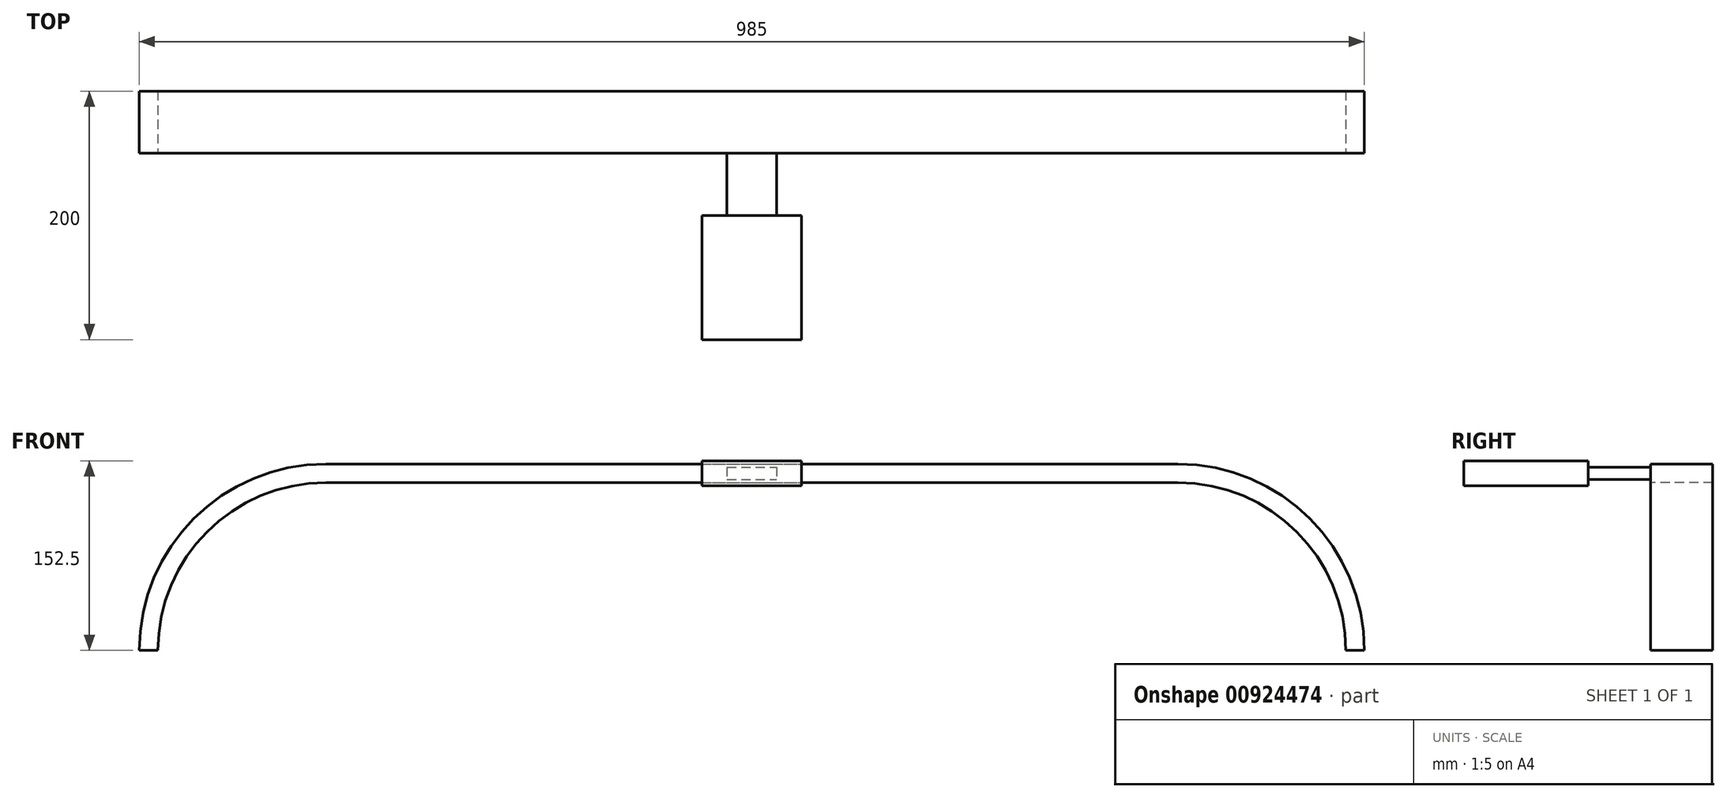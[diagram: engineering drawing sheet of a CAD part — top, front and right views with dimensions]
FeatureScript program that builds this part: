
annotation { "Feature Type Name" : "Feature", "Feature Type Description" : "" }
export const myFeature = defineFeature(function(context is Context, id is Id, definition is map)
    precondition{}
    {
        {
            var Q0;
            Q0=qCreatedBy(makeId("Top.planeOp"),FACE);
            var sketch = newSketch(context, id + "F0", { "sketchPlane" : qUnion([Q0])});
            skLineSegment(sketch, "E0.bottom", {"start": v(-7.5, 25) * mm, "end": v(7.5, 25) * mm});
            skLineSegment(sketch, "E0.top", {"start": v(-7.5, -25) * mm, "end": v(7.5, -25) * mm});
            skLineSegment(sketch, "E0.left", {"start": v(-7.5, 25) * mm, "end": v(-7.5, -25) * mm});
            skLineSegment(sketch, "E0.right", {"start": v(7.5, 25) * mm, "end": v(7.5, -25) * mm});
            skLineSegment(sketch, "E1", {"start": v(-142.5, 39) * mm, "end": v(-142.5, -46.74) * mm});
            skSolve(sketch);
        }
        {
            var Q0;
            Q0=makeQuery(id+"F0.imprint","IMPRINT",FACE,{"disambiguationData":[TD([[makeQuery(id+"F0.imprint","IMPRINT",EDGE,{"derivedFrom":sQuery(id+"F0.wireOp",EDGE,"E0.bottom")}),-1.0]])]});
            var Q1;
            Q1=sQuery(id+"F0.wireOp",EDGE,"E1");
            revolve(context, id + "F1", {"surfaceOperationType" : NewSurfaceOperationType.NEW, "entities" : qUnion([Q0]), "axis" : qUnion([Q1]), "revolveType" : RevolveType.ONE_DIRECTION, "angle" : 90 * degree});
        }
        {
            var Q0;
            Q0=makeQuery(id+"F1.opRevolve","CAP_FACE",FACE,{"disambiguationData":[OSD([sQuery(id+"F0.wireOp",EDGE,"E0.bottom"),sQuery(id+"F0.wireOp",EDGE,"E0.top"),sQuery(id+"F0.wireOp",EDGE,"E0.left"),sQuery(id+"F0.wireOp",EDGE,"E0.right")])],"isStart":false});
            extrude(context, id + "F2", {"entities" : qUnion([Q0]), "operationType" : NewBodyOperationType.ADD, "depth" : 685 * mm, "offsetDistance" : 25 * mm});
        }
        {
            var Q0;
            Q0=makeQuery(id+"F2.opExtrude","CAP_FACE",FACE,{"disambiguationData":[OSD([sQuery(id+"F0.wireOp",EDGE,"E0.bottom"),sQuery(id+"F0.wireOp",EDGE,"E0.top"),sQuery(id+"F0.wireOp",EDGE,"E0.left"),sQuery(id+"F0.wireOp",EDGE,"E0.right")])],"isStart":false});
            var sketch = newSketch(context, id + "F3", { "sketchPlane" : qUnion([Q0])});
            skLineSegment(sketch, "E2", {"start": v(-74.36, 0) * mm, "end": v(76.14, 0) * mm});
            skSolve(sketch);
        }
        {
            var Q0;
            Q0=makeQuery(id+"F3.imprint","IMPRINT",FACE,{"disambiguationData":[TD([[makeQuery(id+"F3.imprint","IMPRINT",EDGE,{"derivedFrom":makeQuery(id+"F2.opExtrude","CAP_EDGE",EDGE,{"disambiguationData":[OSD([sQuery(id+"F0.wireOp",EDGE,"E0.bottom")])],"isStart":false})}),-1.0]])]});
            var Q1;
            Q1=sQuery(id+"F3.wireOp",EDGE,"E2");
            revolve(context, id + "F4", {"operationType" : NewBodyOperationType.ADD, "surfaceOperationType" : NewSurfaceOperationType.NEW, "entities" : qUnion([Q0]), "axis" : qUnion([Q1]), "revolveType" : RevolveType.ONE_DIRECTION, "angle" : 90 * degree});
        }
        {
            var Q0;
            {var subQ0=sQuery(id+"F0.wireOp",EDGE,"E0.top");Q0=makeQuery(id+"F4.boolean.opBoolean","MERGE",FACE,{"derivedFrom":[makeQuery(id+"F2.boolean.opBoolean","MERGE",FACE,{"derivedFrom":[makeQuery(id+"F1.opRevolve","SWEPT_FACE",FACE,{"disambiguationData":[OSD([subQ0])]}),makeQuery(id+"F2.opExtrude","SWEPT_FACE",FACE,{"disambiguationData":[OSD([subQ0])]})]}),makeQuery(id+"F4.opRevolve","SWEPT_FACE",FACE,{"disambiguationData":[OSD([subQ0])]})]});}
            var sketch = newSketch(context, id + "F5", { "sketchPlane" : qUnion([Q0])});
            skLineSegment(sketch, "E3.bottom", {"start": v(-505, 147.5) * mm, "end": v(-465, 147.5) * mm});
            skLineSegment(sketch, "E3.top", {"start": v(-505, 137.5) * mm, "end": v(-465, 137.5) * mm});
            skLineSegment(sketch, "E3.left", {"start": v(-505, 147.5) * mm, "end": v(-505, 137.5) * mm});
            skLineSegment(sketch, "E3.right", {"start": v(-465, 147.5) * mm, "end": v(-465, 137.5) * mm});
            skSolve(sketch);
        }
        {
            var Q0;
            Q0=qSketchRegion(id+"F5",true);
            extrude(context, id + "F6", {"entities" : qUnion([Q0]), "operationType" : NewBodyOperationType.ADD, "depth" : 50 * mm, "offsetDistance" : 25 * mm});
        }
        {
            var Q0;
            Q0=makeQuery(id+"F6.opExtrude","CAP_FACE",FACE,{"disambiguationData":[OSD([sQuery(id+"F5.wireOp",EDGE,"E3.bottom"),sQuery(id+"F5.wireOp",EDGE,"E3.top"),sQuery(id+"F5.wireOp",EDGE,"E3.left"),sQuery(id+"F5.wireOp",EDGE,"E3.right")])],"isStart":false});
            var sketch = newSketch(context, id + "F7", { "sketchPlane" : qUnion([Q0])});
            skLineSegment(sketch, "E4.bottom", {"start": v(-525, 152.5) * mm, "end": v(-445, 152.5) * mm});
            skLineSegment(sketch, "E4.top", {"start": v(-525, 132.5) * mm, "end": v(-445, 132.5) * mm});
            skLineSegment(sketch, "E4.left", {"start": v(-525, 152.5) * mm, "end": v(-525, 132.5) * mm});
            skLineSegment(sketch, "E4.right", {"start": v(-445, 152.5) * mm, "end": v(-445, 132.5) * mm});
            skSolve(sketch);
        }
        {
            var Q0;
            Q0=makeQuery(id+"F7.imprint","IMPRINT",FACE,{"disambiguationData":[TD([[makeQuery(id+"F7.imprint","IMPRINT",EDGE,{"derivedFrom":sQuery(id+"F7.wireOp",EDGE,"E4.bottom")}),-1.0]])]});
            var Q1;
            Q1=makeQuery(id+"F7.imprint","IMPRINT",FACE,{"disambiguationData":[TD([[makeQuery(id+"F7.imprint","IMPRINT",EDGE,{"derivedFrom":makeQuery(id+"F6.opExtrude","CAP_EDGE",EDGE,{"disambiguationData":[OSD([sQuery(id+"F5.wireOp",EDGE,"E3.bottom")])],"isStart":false})}),-1.0]])]});
            extrude(context, id + "F8", {"entities" : qUnion([Q0, Q1]), "depth" : 100 * mm, "offsetDistance" : 25 * mm});
        }
    });
